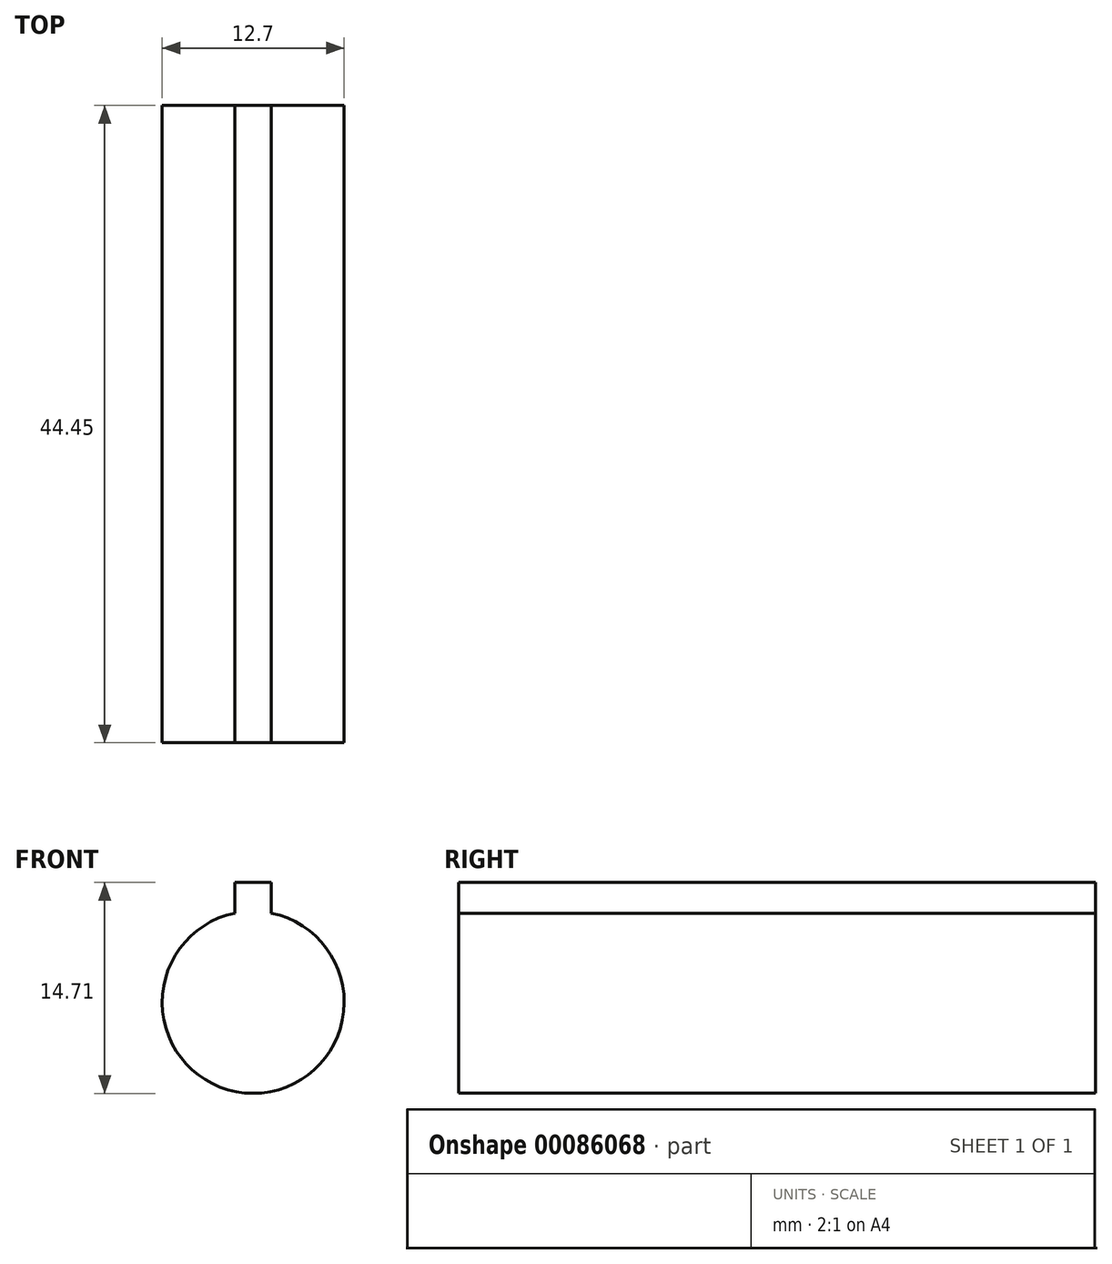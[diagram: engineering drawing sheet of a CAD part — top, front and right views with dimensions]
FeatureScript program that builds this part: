
annotation { "Feature Type Name" : "Feature", "Feature Type Description" : "" }
export const myFeature = defineFeature(function(context is Context, id is Id, definition is map)
    precondition{}
    {
        {
            var Q0;
            Q0=qCreatedBy(makeId("Front.planeOp"),FACE);
            var sketch = newSketch(context, id + "F0", { "sketchPlane" : qUnion([Q0])});
            skArc(sketch, "E0", {"start": v(-21.59, -18.1) * mm, "mid": v(-20.32, -30.67) * mm, "end": v(-19.05, -18.1) * mm});
            skLineSegment(sketch, "E1.bottom", {"start": v(-21.59, -15.96) * mm, "end": v(-19.05, -15.96) * mm});
            skLineSegment(sketch, "E1.left", {"start": v(-21.59, -15.96) * mm, "end": v(-21.59, -18.1) * mm});
            skLineSegment(sketch, "E1.right", {"start": v(-19.05, -15.96) * mm, "end": v(-19.05, -18.1) * mm});
            skPoint(sketch, "E1.top.end.orphan", {"position": v(-19.05, -32.67) * mm});
            skPoint(sketch, "E2.trimOffspring.end.orphan", {"position": v(-21.59, -32.67) * mm});
            skSolve(sketch);
        }
        {
            var Q0;
            Q0=makeQuery(id+"F0.imprint","IMPRINT",FACE,{"disambiguationData":[TD([[makeQuery(id+"F0.imprint","IMPRINT",EDGE,{"derivedFrom":sQuery(id+"F0.wireOp",EDGE,"E0")}),1.0]])]});
            extrude(context, id + "F1", {"entities" : qUnion([Q0]), "depth" : 44.45 * mm});
        }
    });
